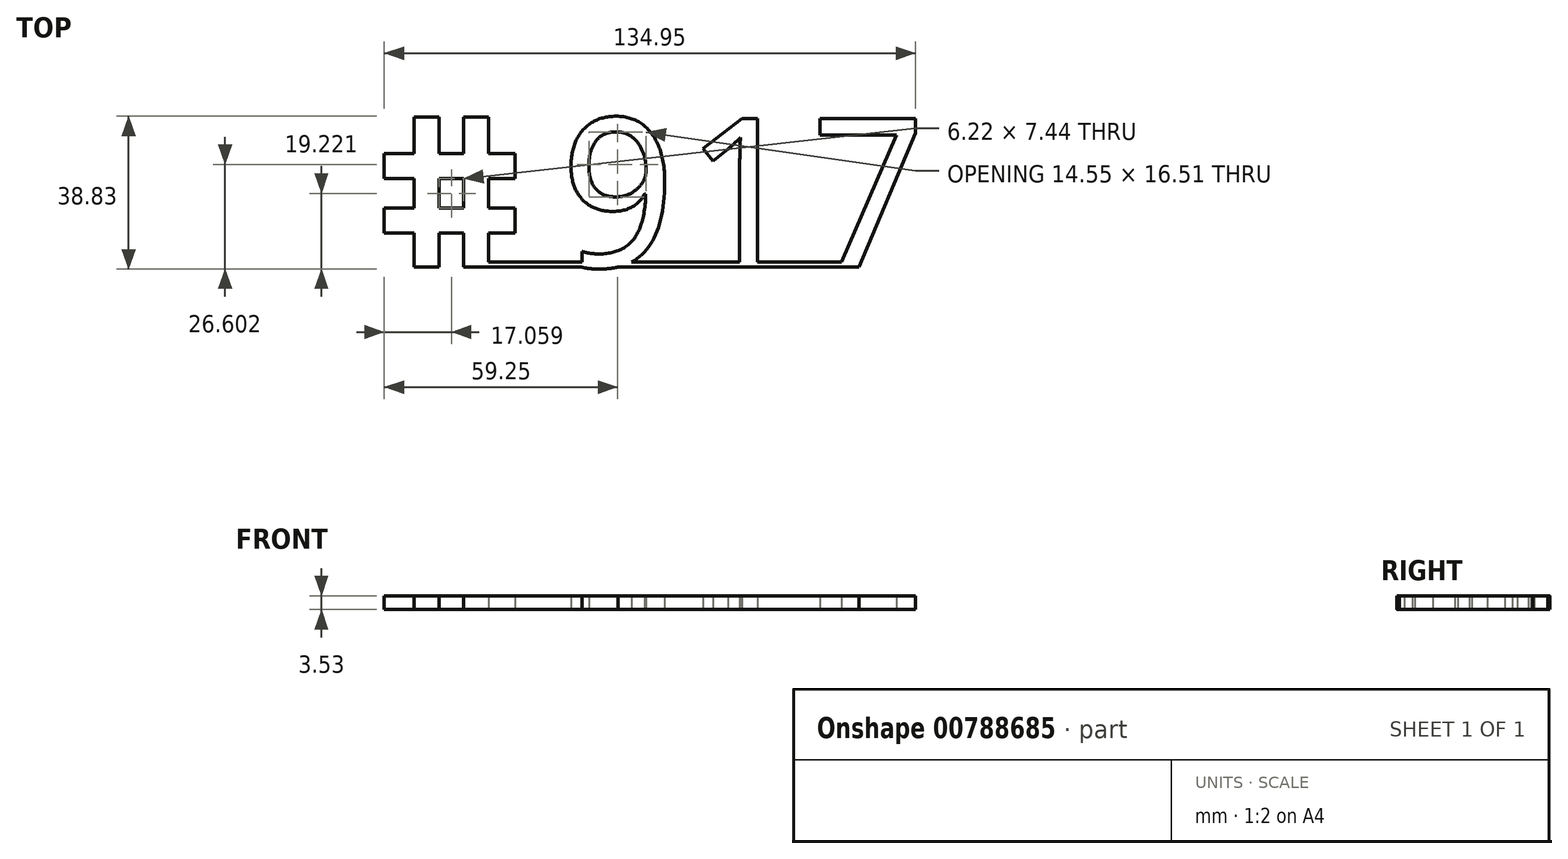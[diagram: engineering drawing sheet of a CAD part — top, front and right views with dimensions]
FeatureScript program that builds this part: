
annotation { "Feature Type Name" : "Feature", "Feature Type Description" : "" }
export const myFeature = defineFeature(function(context is Context, id is Id, definition is map)
    precondition{}
    {
        {
            var Q0;
            Q0=qCreatedBy(makeId("Top.planeOp"),FACE);
            var sketch = newSketch(context, id + "F0", { "sketchPlane" : qUnion([Q0])});
            skLineSegment(sketch, "E0.bottom", {"start": v(-65.53, 23.12) * mm, "end": v(-59.18, 23.12) * mm});
            skLineSegment(sketch, "E0.top", {"start": v(-65.53, -14.98) * mm, "end": v(-59.18, -14.98) * mm});
            skLineSegment(sketch, "E0.left", {"start": v(-65.53, 23.12) * mm, "end": v(-65.53, -14.98) * mm});
            skLineSegment(sketch, "E0.right", {"start": v(-59.18, 23.12) * mm, "end": v(-59.18, -14.98) * mm});
            skLineSegment(sketch, "E1.bottom", {"start": v(-73.13, 13.8) * mm, "end": v(-39.91, 13.8) * mm});
            skLineSegment(sketch, "E1.top", {"start": v(-73.13, 7.44) * mm, "end": v(-39.91, 7.44) * mm});
            skLineSegment(sketch, "E1.left", {"start": v(-73.13, 13.8) * mm, "end": v(-73.13, 7.44) * mm});
            skLineSegment(sketch, "E1.right", {"start": v(-39.91, 13.8) * mm, "end": v(-39.91, 7.44) * mm});
            skLineSegment(sketch, "E2.bottom", {"start": v(-73.13, 0) * mm, "end": v(-39.91, 0) * mm});
            skLineSegment(sketch, "E2.top", {"start": v(-73.13, -6.35) * mm, "end": v(-39.91, -6.35) * mm});
            skLineSegment(sketch, "E2.left", {"start": v(-73.13, 0) * mm, "end": v(-73.13, -6.35) * mm});
            skLineSegment(sketch, "E2.right", {"start": v(-39.91, 0) * mm, "end": v(-39.91, -6.35) * mm});
            skLineSegment(sketch, "E3.bottom", {"start": v(-52.96, 23.12) * mm, "end": v(-46.61, 23.12) * mm});
            skLineSegment(sketch, "E3.top", {"start": v(-52.96, -14.98) * mm, "end": v(-46.61, -14.98) * mm});
            skLineSegment(sketch, "E3.left", {"start": v(-52.96, 23.12) * mm, "end": v(-52.96, -14.98) * mm});
            skLineSegment(sketch, "E3.right", {"start": v(-46.61, 23.12) * mm, "end": v(-46.61, -14.98) * mm});
            skText(sketch, "E4", { "text": "917", "fontName": "DroidSansMono.ttf"});
            skLineSegment(sketch, "E5.bottom", {"start": v(-46.61, -14.98) * mm, "end": v(47.5, -14.98) * mm});
            skLineSegment(sketch, "E5.top", {"start": v(-46.61, -13.68) * mm, "end": v(47.5, -13.68) * mm});
            skLineSegment(sketch, "E5.left", {"start": v(-46.61, -14.98) * mm, "end": v(-46.61, -13.68) * mm});
            skLineSegment(sketch, "E5.right", {"start": v(47.5, -14.98) * mm, "end": v(47.5, -13.68) * mm});
            const initialGuessF0  = {"E4": [-0.02968, -0.01498, 1, 0, 0.0381]};
            skSetInitialGuess(sketch, initialGuessF0);
            skSolve(sketch);
        }
        {
            var Q0;
            {var subQ0=sQuery(id+"F0.wireOp",EDGE,"E5.top");var subQ1=sQuery(id+"F0.wireOp",EDGE,"E4.sketch_text.stroke-31");var subQ2=makeQuery(id+"F0.imprint","INTERSECT",VERTEX,{"derivedFrom":[subQ1,subQ0]});var subQ3=sQuery(id+"F0.wireOp",EDGE,"E5.right");var subQ6=sQuery(id+"F0.wireOp",EDGE,"E4.sketch_text.stroke-37");var subQ7=sQuery(id+"F0.wireOp",EDGE,"E5.bottom");var subQ15=sQuery(id+"F0.wireOp",EDGE,"E3.left");var subQ16=sQuery(id+"F0.wireOp",EDGE,"E1.bottom");var subQ17=makeQuery(id+"F0.imprint","INTERSECT",VERTEX,{"derivedFrom":[subQ16,subQ15]});var subQ20=makeQuery(id+"F0.imprint","IMPRINT",EDGE,{"disambiguationData":[TD([[subQ17,-1.0]])],"derivedFrom":subQ16});var subQ21=sQuery(id+"F0.wireOp",EDGE,"E3.bottom");var subQ22=sQuery(id+"F0.wireOp",EDGE,"E0.left");var subQ23=makeQuery(id+"F0.imprint","INTERSECT",VERTEX,{"derivedFrom":[subQ22,subQ16]});var subQ24=sQuery(id+"F0.wireOp",EDGE,"E1.top");var subQ25=makeQuery(id+"F0.imprint","INTERSECT",VERTEX,{"derivedFrom":[subQ22,subQ24]});var subQ26=makeQuery(id+"F0.imprint","IMPRINT",EDGE,{"disambiguationData":[TD([[subQ23,-1.0]])],"derivedFrom":subQ22});var subQ27=sQuery(id+"F0.wireOp",EDGE,"E0.right");var subQ28=makeQuery(id+"F0.imprint","INTERSECT",VERTEX,{"derivedFrom":[subQ27,subQ16]});var subQ30=makeQuery(id+"F0.imprint","IMPRINT",EDGE,{"disambiguationData":[TD([[subQ28,-1.0]])],"derivedFrom":subQ27});var subQ33=sQuery(id+"F0.wireOp",EDGE,"E1.right");var subQ36=sQuery(id+"F0.wireOp",EDGE,"E2.top");var subQ37=makeQuery(id+"F0.imprint","INTERSECT",VERTEX,{"derivedFrom":[subQ22,subQ36]});var subQ38=sQuery(id+"F0.wireOp",EDGE,"E2.bottom");var subQ40=makeQuery(id+"F0.imprint","IMPRINT",EDGE,{"disambiguationData":[TD([[subQ37,1.0]])],"derivedFrom":subQ22});var subQ41=makeQuery(id+"F0.imprint","INTERSECT",VERTEX,{"derivedFrom":[subQ27,subQ36]});var subQ43=makeQuery(id+"F0.imprint","IMPRINT",EDGE,{"disambiguationData":[TD([[subQ41,1.0]])],"derivedFrom":subQ27});var subQ46=sQuery(id+"F0.wireOp",EDGE,"E2.left");var subQ47=sQuery(id+"F0.wireOp",EDGE,"E1.left");var subQ48=makeQuery(id+"F0.imprint","INTERSECT",VERTEX,{"derivedFrom":[subQ24,subQ15]});var subQ49=makeQuery(id+"F0.imprint","IMPRINT",EDGE,{"disambiguationData":[TD([[subQ48,-1.0]])],"derivedFrom":subQ24});var subQ51=sQuery(id+"F0.wireOp",EDGE,"E0.top");var subQ52=makeQuery(id+"F0.imprint","INTERSECT",VERTEX,{"derivedFrom":[subQ38,subQ15]});var subQ54=makeQuery(id+"F0.imprint","IMPRINT",EDGE,{"disambiguationData":[TD([[subQ52,-1.0]])],"derivedFrom":subQ38});var subQ60=sQuery(id+"F0.wireOp",EDGE,"E0.bottom");var subQ61=sQuery(id+"F0.wireOp",EDGE,"E4.sketch_text.stroke-0");var subQ62=makeQuery(id+"F0.imprint","INTERSECT",VERTEX,{"derivedFrom":[subQ61,subQ0]});var subQ64=makeQuery(id+"F0.imprint","IMPRINT",EDGE,{"disambiguationData":[TD([[subQ62,1.0]])],"derivedFrom":subQ61});var subQ65=sQuery(id+"F0.wireOp",EDGE,"E4.sketch_text.stroke-12");var subQ66=makeQuery(id+"F0.imprint","INTERSECT",VERTEX,{"derivedFrom":[subQ65,subQ7]});var subQ68=makeQuery(id+"F0.imprint","IMPRINT",EDGE,{"disambiguationData":[TD([[subQ66,1.0]])],"derivedFrom":subQ65});var subQ72=sQuery(id+"F0.wireOp",EDGE,"E3.top");var subQ75=makeQuery(id+"F0.imprint","INTERSECT",VERTEX,{"derivedFrom":[subQ7,subQ3]});var subQ77=sQuery(id+"F0.wireOp",EDGE,"E4.sketch_text.stroke-22");var subQ81=sQuery(id+"F0.wireOp",EDGE,"E4.sketch_text.stroke-1");var subQ83=sQuery(id+"F0.wireOp",EDGE,"E4.sketch_text.stroke-32");var subQ85=sQuery(id+"F0.wireOp",EDGE,"E4.sketch_text.stroke-24");var subQ92=sQuery(id+"F0.wireOp",EDGE,"E4.sketch_text.stroke-13");var subQ93=sQuery(id+"F0.wireOp",EDGE,"E2.right");Q0=qUnion([makeQuery(id+"F0.imprint","IMPRINT",FACE,{"disambiguationData":[TD([[makeQuery(id+"F0.imprint","IMPRINT",EDGE,{"derivedFrom":subQ77}),-1.0]])]}),makeQuery(id+"F0.imprint","IMPRINT",FACE,{"disambiguationData":[TD([[makeQuery(id+"F0.imprint","IMPRINT",EDGE,{"derivedFrom":subQ93}),-1.0]])]}),makeQuery(id+"F0.imprint","IMPRINT",FACE,{"disambiguationData":[TD([[subQ49,-1.0]])]}),makeQuery(id+"F0.imprint","IMPRINT",FACE,{"disambiguationData":[TD([[makeQuery(id+"F0.imprint","IMPRINT",EDGE,{"derivedFrom":subQ92}),-1.0]])]}),makeQuery(id+"F0.imprint","IMPRINT",FACE,{"disambiguationData":[TD([[subQ43,1.0]])]}),makeQuery(id+"F0.imprint","IMPRINT",FACE,{"disambiguationData":[TD([[subQ68,1.0]])]}),makeQuery(id+"F0.imprint","IMPRINT",FACE,{"disambiguationData":[TD([[subQ30,1.0]])]}),makeQuery(id+"F0.imprint","IMPRINT",FACE,{"disambiguationData":[TD([[makeQuery(id+"F0.imprint","IMPRINT",EDGE,{"derivedFrom":subQ85}),-1.0]])]}),makeQuery(id+"F0.imprint","IMPRINT",FACE,{"disambiguationData":[TD([[subQ64,1.0]])]}),makeQuery(id+"F0.imprint","IMPRINT",FACE,{"disambiguationData":[TD([[makeQuery(id+"F0.imprint","IMPRINT",EDGE,{"disambiguationData":[TD([[subQ25,-1.0]])],"derivedFrom":subQ22}),1.0]])]}),makeQuery(id+"F0.imprint","IMPRINT",FACE,{"disambiguationData":[TD([[makeQuery(id+"F0.imprint","IMPRINT",EDGE,{"derivedFrom":subQ83}),-1.0]])]}),makeQuery(id+"F0.imprint","IMPRINT",FACE,{"disambiguationData":[TD([[makeQuery(id+"F0.imprint","IMPRINT",EDGE,{"derivedFrom":subQ81}),-1.0]])]}),makeQuery(id+"F0.imprint","IMPRINT",FACE,{"disambiguationData":[TD([[makeQuery(id+"F0.imprint","IMPRINT",EDGE,{"disambiguationData":[TD([[subQ2,1.0]])],"derivedFrom":subQ0}),-1.0]])]}),makeQuery(id+"F0.imprint","IMPRINT",FACE,{"disambiguationData":[TD([[makeQuery(id+"F0.imprint","IMPRINT",EDGE,{"disambiguationData":[TD([[subQ75,-1.0]])],"derivedFrom":subQ3}),1.0]])]}),makeQuery(id+"F0.imprint","IMPRINT",FACE,{"disambiguationData":[TD([[makeQuery(id+"F0.imprint","IMPRINT",EDGE,{"derivedFrom":subQ72}),1.0]])]}),makeQuery(id+"F0.imprint","IMPRINT",FACE,{"disambiguationData":[TD([[subQ64,-1.0]])]}),makeQuery(id+"F0.imprint","IMPRINT",FACE,{"disambiguationData":[TD([[makeQuery(id+"F0.imprint","IMPRINT",EDGE,{"derivedFrom":subQ60}),-1.0]])]}),makeQuery(id+"F0.imprint","IMPRINT",FACE,{"disambiguationData":[TD([[subQ54,-1.0]])]}),makeQuery(id+"F0.imprint","IMPRINT",FACE,{"disambiguationData":[TD([[makeQuery(id+"F0.imprint","IMPRINT",EDGE,{"derivedFrom":subQ51}),1.0]])]}),makeQuery(id+"F0.imprint","IMPRINT",FACE,{"disambiguationData":[TD([[subQ20,-1.0]])]}),makeQuery(id+"F0.imprint","IMPRINT",FACE,{"disambiguationData":[TD([[makeQuery(id+"F0.imprint","IMPRINT",EDGE,{"derivedFrom":subQ47}),1.0]])]}),makeQuery(id+"F0.imprint","IMPRINT",FACE,{"disambiguationData":[TD([[makeQuery(id+"F0.imprint","IMPRINT",EDGE,{"derivedFrom":subQ46}),1.0]])]}),makeQuery(id+"F0.imprint","IMPRINT",FACE,{"disambiguationData":[TD([[subQ40,1.0]])]}),makeQuery(id+"F0.imprint","IMPRINT",FACE,{"disambiguationData":[TD([[makeQuery(id+"F0.imprint","IMPRINT",EDGE,{"derivedFrom":subQ33}),-1.0]])]}),makeQuery(id+"F0.imprint","IMPRINT",FACE,{"disambiguationData":[TD([[subQ26,1.0]])]}),makeQuery(id+"F0.imprint","IMPRINT",FACE,{"disambiguationData":[TD([[makeQuery(id+"F0.imprint","IMPRINT",EDGE,{"derivedFrom":subQ21}),-1.0]])]}),makeQuery(id+"F0.imprint","IMPRINT",FACE,{"disambiguationData":[TD([[makeQuery(id+"F0.imprint","IMPRINT",EDGE,{"derivedFrom":subQ6}),-1.0]])]})]);}
            extrude(context, id + "F1", {"entities" : qUnion([Q0]), "depth" : 3.53 * mm, "offsetDistance" : 25.4 * mm});
        }
    });
